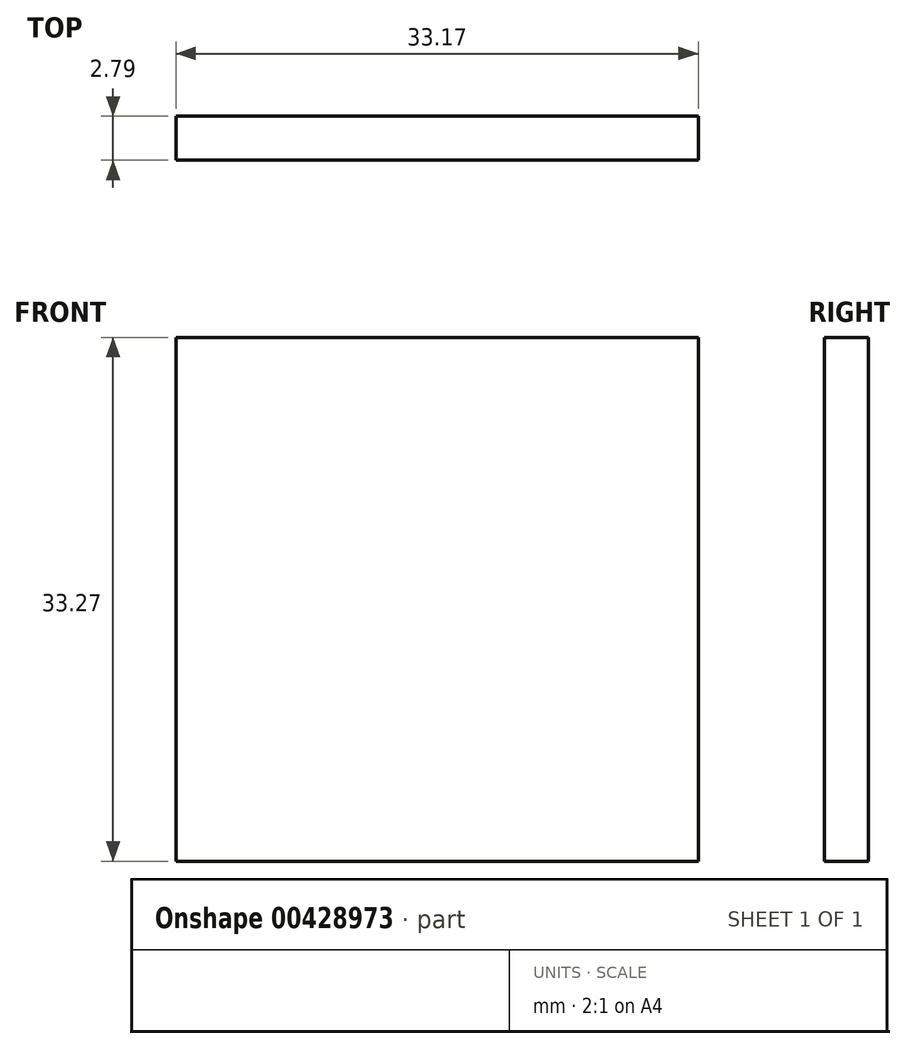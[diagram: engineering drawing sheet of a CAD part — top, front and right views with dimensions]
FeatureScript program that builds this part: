
annotation { "Feature Type Name" : "Feature", "Feature Type Description" : "" }
export const myFeature = defineFeature(function(context is Context, id is Id, definition is map)
    precondition{}
    {
        {
            var Q0;
            Q0=qCreatedBy(makeId("Front.planeOp"),FACE);
            var sketch = newSketch(context, id + "F0", { "sketchPlane" : qUnion([Q0])});
            skLineSegment(sketch, "E0.bottom", {"start": v(0, 0) * mm, "end": v(33.17, 0) * mm});
            skLineSegment(sketch, "E0.top", {"start": v(0, 33.27) * mm, "end": v(33.17, 33.27) * mm});
            skLineSegment(sketch, "E0.left", {"start": v(0, 0) * mm, "end": v(0, 33.27) * mm});
            skLineSegment(sketch, "E0.right", {"start": v(33.17, 0) * mm, "end": v(33.17, 33.27) * mm});
            skSolve(sketch);
        }
        {
            var Q0;
            Q0=makeQuery(id+"F0.imprint","IMPRINT",FACE,{"disambiguationData":[TD([[makeQuery(id+"F0.imprint","IMPRINT",EDGE,{"derivedFrom":sQuery(id+"F0.wireOp",EDGE,"E0.bottom")}),1.0]])]});
            extrude(context, id + "F1", {"entities" : qUnion([Q0]), "oppositeDirection" : true, "depth" : 2.8 * mm});
        }
    });
